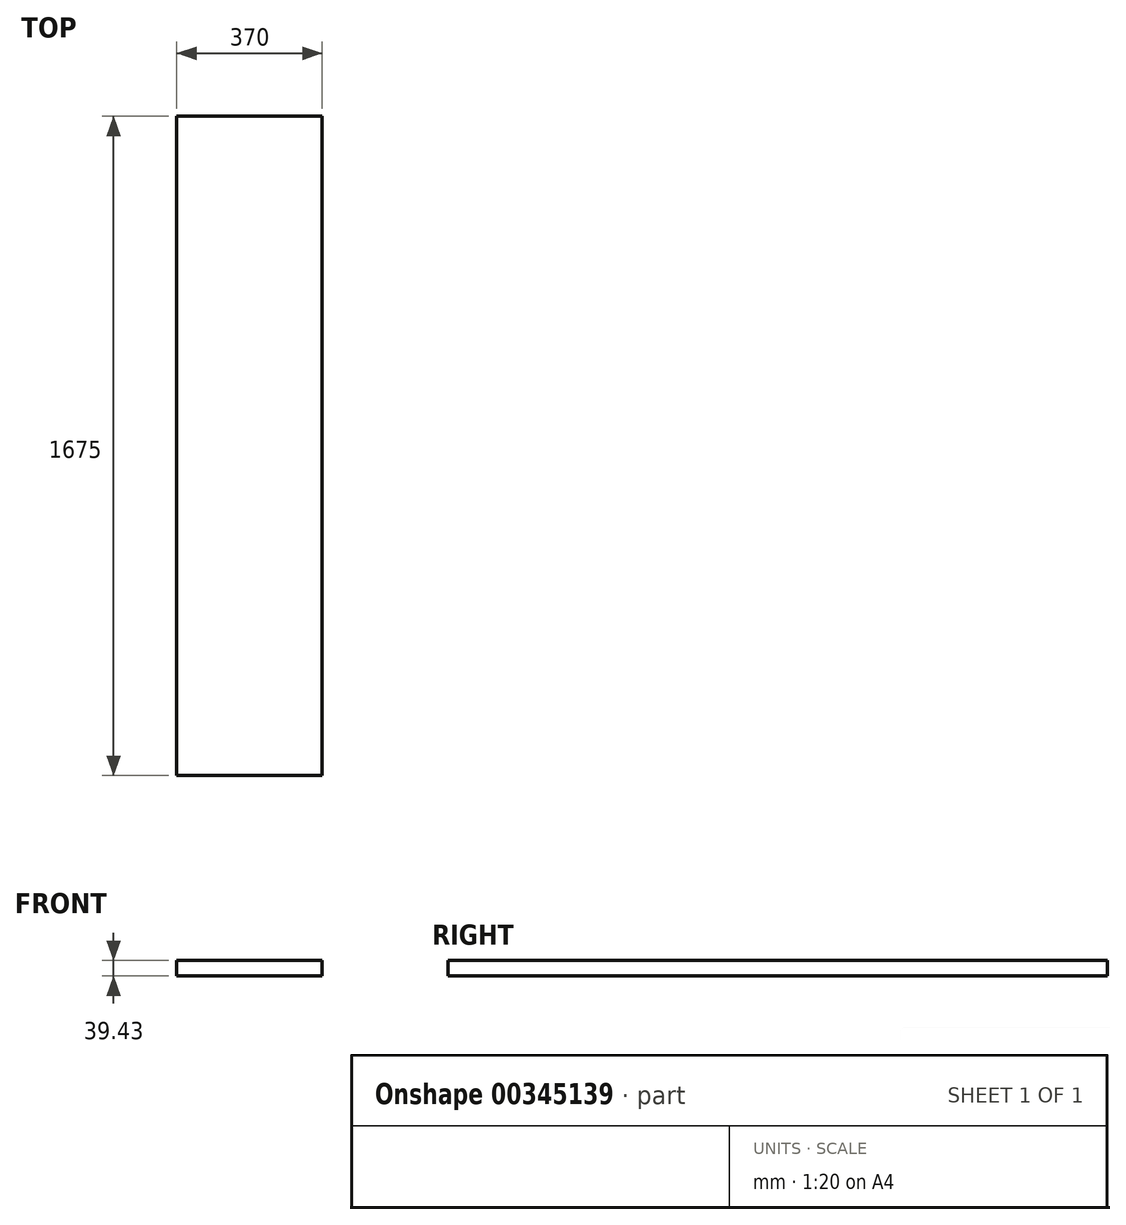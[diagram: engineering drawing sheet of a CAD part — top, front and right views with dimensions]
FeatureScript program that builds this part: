
annotation { "Feature Type Name" : "Feature", "Feature Type Description" : "" }
export const myFeature = defineFeature(function(context is Context, id is Id, definition is map)
    precondition{}
    {
        {
            var Q0;
            Q0=qCreatedBy(makeId("Right.planeOp"),FACE);
            var sketch = newSketch(context, id + "F0", { "sketchPlane" : qUnion([Q0])});
            skLineSegment(sketch, "E0.bottom", {"start": v(0, 0) * mm, "end": v(-48.45, 0) * mm});
            skLineSegment(sketch, "E0.top", {"start": v(0, 39.43) * mm, "end": v(-48.45, 39.43) * mm});
            skLineSegment(sketch, "E0.left", {"start": v(0, 0) * mm, "end": v(0, 39.43) * mm});
            skLineSegment(sketch, "E0.right", {"start": v(-48.45, 0) * mm, "end": v(-48.45, 39.43) * mm});
            skSolve(sketch);
        }
        {
            var Q0;
            Q0=makeQuery(id+"F0.imprint","IMPRINT",FACE,{"disambiguationData":[TD([[makeQuery(id+"F0.imprint","IMPRINT",EDGE,{"derivedFrom":sQuery(id+"F0.wireOp",EDGE,"E0.bottom")}),-1.0]])]});
            extrude(context, id + "F1", {"entities" : qUnion([Q0]), "oppositeDirection" : true, "depth" : 600 * mm});
        }
        {
            var Q0;
            Q0=makeQuery(id+"F1.opExtrude","SWEPT_FACE",FACE,{"disambiguationData":[OSD([sQuery(id+"F0.wireOp",EDGE,"E0.left")])]});
            extrude(context, id + "F2", {"entities" : qUnion([Q0]), "operationType" : NewBodyOperationType.ADD, "oppositeDirection" : true, "depth" : 1700 * mm});
        }
        {
            var Q0;
            Q0=makeQuery(id+"F2.opExtrude","CAP_FACE",FACE,{"disambiguationData":[OSD([sQuery(id+"F0.wireOp",EDGE,"E0.left")])],"isStart":false});
            extrude(context, id + "F3", {"entities" : qUnion([Q0]), "operationType" : NewBodyOperationType.REMOVE, "oppositeDirection" : true, "depth" : 25 * mm});
        }
        {
            var Q0;
            {var subQ0=sQuery(id+"F0.wireOp",EDGE,"E0.left");Q0=makeQuery(id+"F2.boolean.opBoolean","MERGE",FACE,{"derivedFrom":[makeQuery(id+"F1.opExtrude","CAP_FACE",FACE,{"disambiguationData":[OSD([sQuery(id+"F0.wireOp",EDGE,"E0.bottom"),sQuery(id+"F0.wireOp",EDGE,"E0.top"),subQ0,sQuery(id+"F0.wireOp",EDGE,"E0.right")])],"isStart":false}),makeQuery(id+"F2.opExtrude","SWEPT_FACE",FACE,{"disambiguationData":[OSD([subQ0]),TDD([makeQuery(id+"F1.opExtrude","CAP_EDGE",EDGE,{"disambiguationData":[OSD([subQ0])],"isStart":false})])]})]});}
            extrude(context, id + "F4", {"entities" : qUnion([Q0]), "operationType" : NewBodyOperationType.REMOVE, "oppositeDirection" : true, "depth" : 230 * mm});
        }
    });
